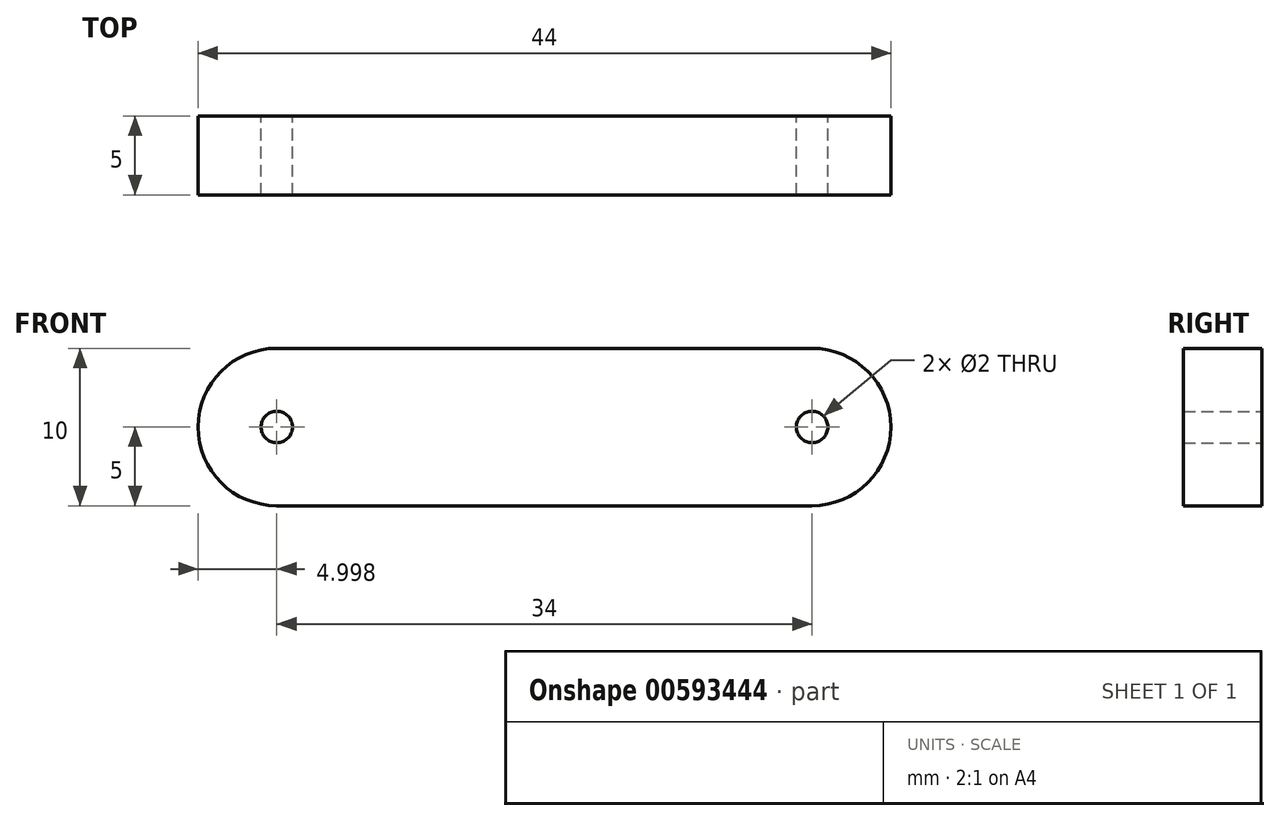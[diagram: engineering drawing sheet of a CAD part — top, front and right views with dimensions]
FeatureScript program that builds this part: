
annotation { "Feature Type Name" : "Feature", "Feature Type Description" : "" }
export const myFeature = defineFeature(function(context is Context, id is Id, definition is map)
    precondition{}
    {
        {
            assignVariable(context, id + "F0", {"name" : "bar_hole", "anyValue" : 2});
        }
        {
            assignVariable(context, id + "F1", {"name" : "Bar_depth", "anyValue" : 5});
        }
        {
            var Q0;
            Q0=qCreatedBy(makeId("Front.planeOp"),FACE);
            var sketch = newSketch(context, id + "F2", { "sketchPlane" : qUnion([Q0])});
            skLineSegment(sketch, "E0", {"start": v(-27.71, 0) * mm, "end": v(34.66, 0) * mm, "construction": true});
            skLineSegment(sketch, "E1", {"start": v(-23.42, 5) * mm, "end": v(10.58, 5) * mm});
            skLineSegment(sketch, "E2.MirrorCS", {"start": v(-23.42, -5) * mm, "end": v(10.58, -5) * mm});
            skCircle(sketch, "E3", {"center": v(-23.42, 0) * mm, "radius": 5 * mm});
            skLineSegment(sketch, "E4", {"start": v(-6.42, 5) * mm, "end": v(-6.42, -16.76) * mm, "construction": true});
            skCircle(sketch, "E5.MirrorC", {"center": v(10.58, 0) * mm, "radius": 5 * mm});
            skSolve(sketch);
        }
        {
            var Q0;
            Q0 = qSketchRegion(id + "F2", true);
            extrude(context, id + "F3", {"entities" : qUnion([Q0]), "depth" : (getVariable(context, 'Bar_depth')) * mm, "offsetDistance" : 25 * mm});
        }
        {
            var Q0;
            Q0=sQuery(id+"F2.wireOp",VERTEX,"E3.center");
            var Q1;
            Q1=sQuery(id+"F2.wireOp",VERTEX,"E5.MirrorC.center");
            var Q2;
            Q2=makeQuery(id+"F3.opExtrude","SWEPT_BODY",BODY,{"disambiguationData":[OSD([sQuery(id+"F2.wireOp",EDGE,"E1"),sQuery(id+"F2.wireOp",EDGE,"E2.MirrorCS"),sQuery(id+"F2.wireOp",EDGE,"E3"),sQuery(id+"F2.wireOp",EDGE,"E5.MirrorC")])]});
            hole(context, id + "F4", {"style" : HoleStyle.SIMPLE, "endStyle" : HoleEndStyle.THROUGH, "oppositeDirection" : true, "holeDiameter" : (getVariable(context, 'bar_hole')) * mm, "majorDiameter" : 5 * mm, "isTappedThrough" : true, "tappedDepth" : 12.7 * mm, "tapClearance" : 3, "locations" : qUnion([Q0, Q1]), "scope" : qUnion([Q2])});
        }
    });
